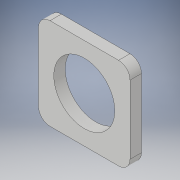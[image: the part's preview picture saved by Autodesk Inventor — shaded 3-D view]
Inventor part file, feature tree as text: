
AUTODESK INVENTOR PART (.ipt)
format: ipt  version: 2018 (Build 220112000, 112)  size: 110,080 bytes
history: native  units: in
note: dims shown in document units (in); Inventor stores cm internally (conversion verified against a paired STEP export)
features: extrude x1, fillet x1, sketch x1
ambient origin geometry x8: Origin, YZ Plane, XZ Plane, XY Plane, X Axis, Y Axis, Z Axis, Center Point
bodies: Solid1 (feature_tree)
feature tree (3):
  extrude  "Extrusion1"  Depth=4.0in
  fillet  "Fillet1"  Radius=4.0in
  sketch  "Sketch1"  dims[d0=2.67in d1=4.0in d2=4.0in d3=0.5in d4=0.0in d5=0.5in]
